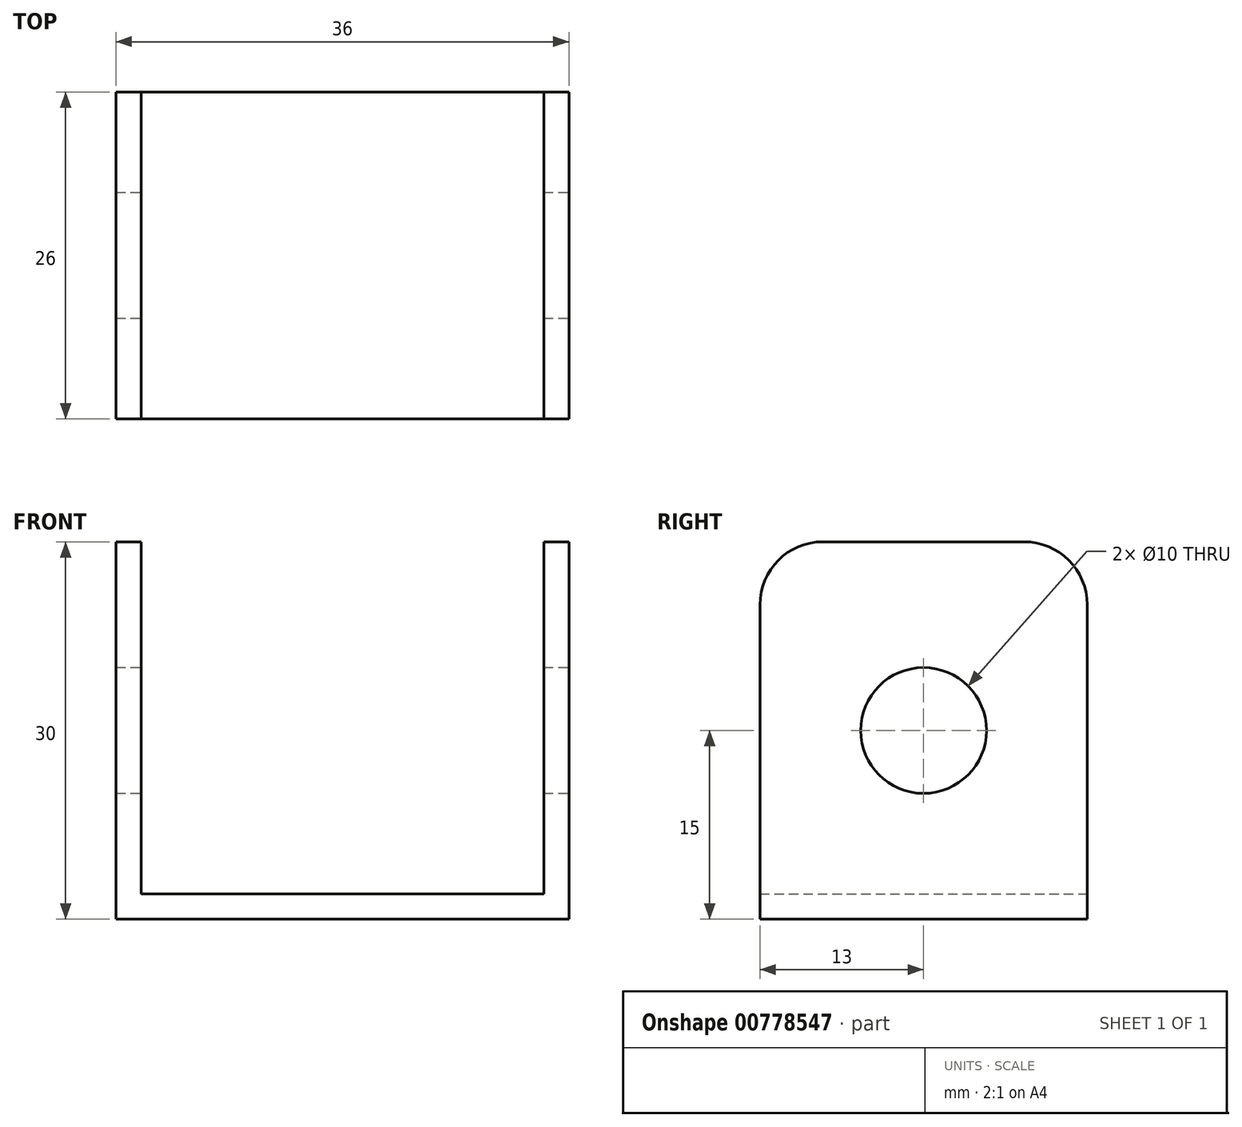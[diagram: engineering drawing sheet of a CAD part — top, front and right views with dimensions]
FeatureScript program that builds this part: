
annotation { "Feature Type Name" : "Feature", "Feature Type Description" : "" }
export const myFeature = defineFeature(function(context is Context, id is Id, definition is map)
    precondition{}
    {
        {
            var Q0;
            Q0=qCreatedBy(makeId("Front.planeOp"),FACE);
            var sketch = newSketch(context, id + "F0", { "sketchPlane" : qUnion([Q0])});
            skLineSegment(sketch, "E0", {"start": v(0, 0) * mm, "end": v(-36, 0) * mm});
            skLineSegment(sketch, "E1", {"start": v(-36, 0) * mm, "end": v(-36, 30) * mm});
            skLineSegment(sketch, "E2", {"start": v(0, 0) * mm, "end": v(0, 30) * mm});
            skLineSegment(sketch, "E3", {"start": v(0, 30) * mm, "end": v(-2, 30) * mm});
            skLineSegment(sketch, "E4", {"start": v(-2, 30) * mm, "end": v(-2, 2) * mm});
            skLineSegment(sketch, "E5", {"start": v(-2, 2) * mm, "end": v(-34, 2) * mm});
            skLineSegment(sketch, "E6", {"start": v(-34, 2) * mm, "end": v(-34, 30) * mm});
            skLineSegment(sketch, "E7", {"start": v(-34, 30) * mm, "end": v(-36, 30) * mm});
            skSolve(sketch);
        }
        {
            var Q0;
            Q0=makeQuery(id+"F0.imprint","IMPRINT",FACE,{"disambiguationData":[TD([[makeQuery(id+"F0.imprint","IMPRINT",EDGE,{"derivedFrom":sQuery(id+"F0.wireOp",EDGE,"E0")}),-1.0]])]});
            extrude(context, id + "F1", {"entities" : qUnion([Q0]), "depth" : 26 * mm, "offsetDistance" : 25 * mm});
        }
        {
            var Q0;
            Q0=makeQuery(id+"F1.opExtrude","SWEPT_FACE",FACE,{"disambiguationData":[OSD([sQuery(id+"F0.wireOp",EDGE,"E2")])]});
            var sketch = newSketch(context, id + "F2", { "sketchPlane" : qUnion([Q0])});
            skCircle(sketch, "E8", {"center": v(-13, 15) * mm, "radius": 5 * mm});
            skPoint(sketch, "E8.centerSnap0", {"position": v(-13, 30) * mm});
            skPoint(sketch, "E8.centerSnap1", {"position": v(-26, 15) * mm});
            skSolve(sketch);
        }
        {
            var Q0;
            Q0=makeQuery(id+"F2.imprint","IMPRINT",FACE,{"disambiguationData":[TD([[makeQuery(id+"F2.imprint","IMPRINT",EDGE,{"derivedFrom":sQuery(id+"F2.wireOp",EDGE,"E8")}),1.0]])]});
            extrude(context, id + "F3", {"entities" : qUnion([Q0]), "operationType" : NewBodyOperationType.REMOVE, "oppositeDirection" : true, "depth" : 52.2 * mm, "offsetDistance" : 25 * mm});
        }
        {
            var Q0;
            Q0=makeQuery(id+"F1.opExtrude","CAP_EDGE",EDGE,{"disambiguationData":[OSD([sQuery(id+"F0.wireOp",EDGE,"E3")])],"isStart":true});
            var Q1;
            Q1=makeQuery(id+"F1.opExtrude","CAP_EDGE",EDGE,{"disambiguationData":[OSD([sQuery(id+"F0.wireOp",EDGE,"E3")])],"isStart":false});
            var Q2;
            Q2=makeQuery(id+"F1.opExtrude","CAP_EDGE",EDGE,{"disambiguationData":[OSD([sQuery(id+"F0.wireOp",EDGE,"E7")])],"isStart":true});
            var Q3;
            Q3=makeQuery(id+"F1.opExtrude","CAP_EDGE",EDGE,{"disambiguationData":[OSD([sQuery(id+"F0.wireOp",EDGE,"E7")])],"isStart":false});
            fillet(context, id + "F4", {"entities" : qUnion([Q0, Q1, Q2, Q3]), "radius" : 5 * mm, "tangentPropagation" : true, "allowEdgeOverflow" : false});
        }
    });
